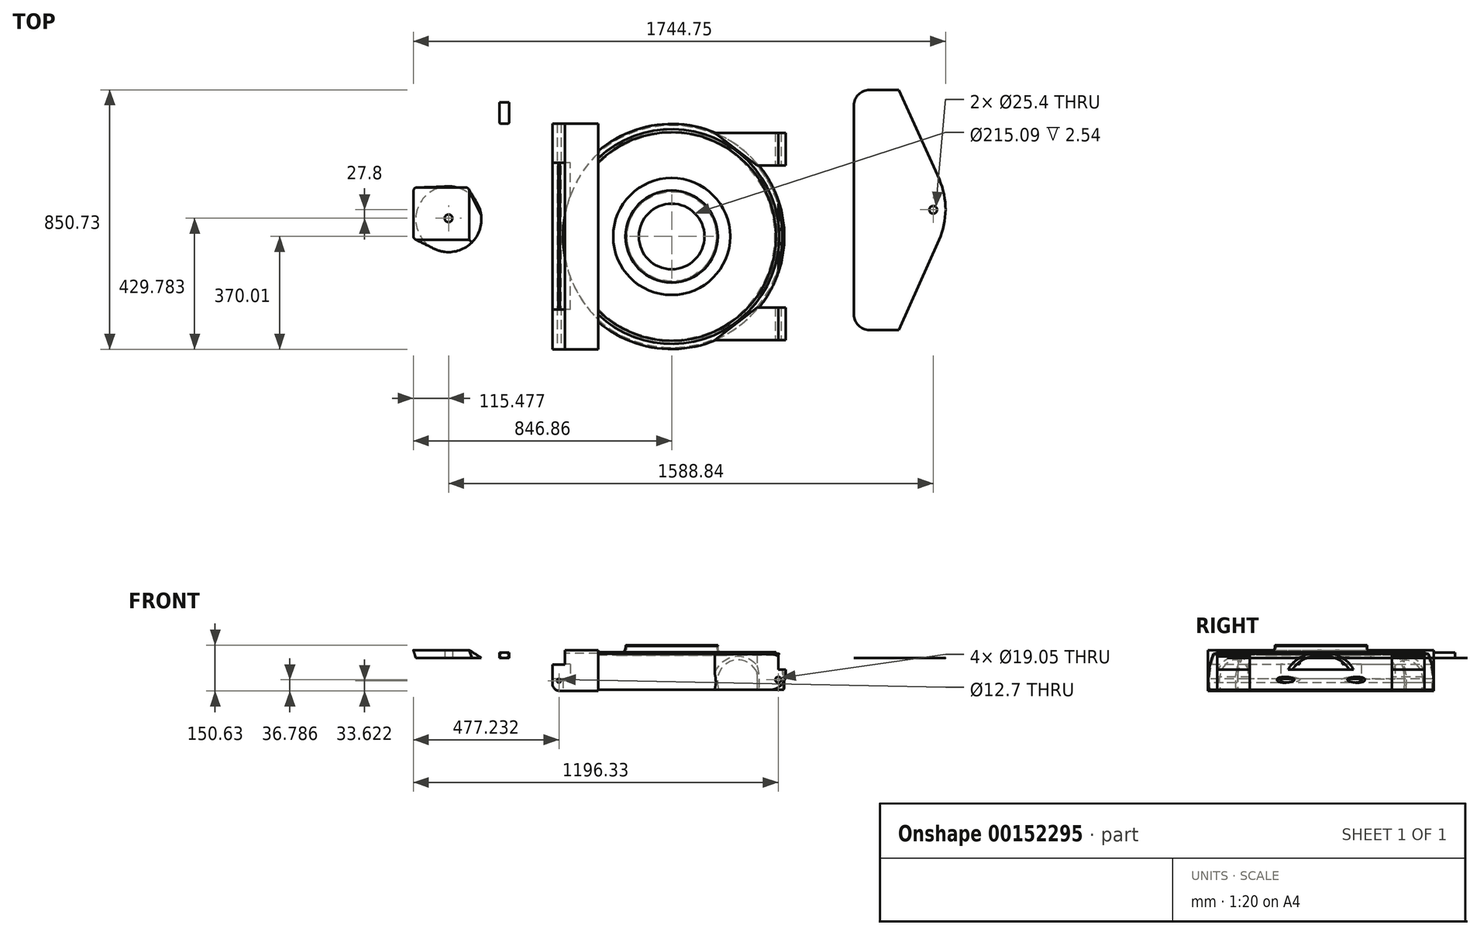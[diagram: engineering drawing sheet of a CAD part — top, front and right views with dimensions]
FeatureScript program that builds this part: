
annotation { "Feature Type Name" : "Feature", "Feature Type Description" : "" }
export const myFeature = defineFeature(function(context is Context, id is Id, definition is map)
    precondition{}
    {
        {
            var Q0;
            Q0=qCreatedBy(makeId("Front.planeOp"),FACE);
            var sketch = newSketch(context, id + "F0", { "sketchPlane" : qUnion([Q0])});
            skArc(sketch, "E0", {"start": v(88.44, -104.18) * mm, "mid": v(87.74, -44.08) * mm, "end": v(72.73, 14.12) * mm});
            skLineSegment(sketch, "E1", {"start": v(72.73, 14.12) * mm, "end": v(62.92, 14.12) * mm});
            skLineSegment(sketch, "E2", {"start": v(62.92, 14.12) * mm, "end": v(62.92, 19.16) * mm});
            skLineSegment(sketch, "E3", {"start": v(62.92, 19.16) * mm, "end": v(-87.54, 19.16) * mm});
            skArc(sketch, "E4", {"start": v(-127.97, 39.68) * mm, "mid": v(-115.17, 14.8) * mm, "end": v(-87.54, 19.16) * mm});
            skArc(sketch, "E5.0", {"start": v(84.66, -103.77) * mm, "mid": v(84.13, -45.87) * mm, "end": v(70.11, 10.3) * mm});
            skArc(sketch, "E5.1", {"start": v(-131.82, 39.68) * mm, "mid": v(-117.36, 11.64) * mm, "end": v(-86.03, 15.35) * mm});
            skLineSegment(sketch, "E5.2", {"start": v(59.1, 15.35) * mm, "end": v(-86.03, 15.35) * mm});
            skLineSegment(sketch, "E5.3", {"start": v(59.1, 10.3) * mm, "end": v(59.1, 15.35) * mm});
            skLineSegment(sketch, "E5.4", {"start": v(70.11, 10.3) * mm, "end": v(59.1, 10.3) * mm});
            skLineSegment(sketch, "E6", {"start": v(84.66, -103.77) * mm, "end": v(88.44, -104.18) * mm});
            skLineSegment(sketch, "E7", {"start": v(-127.97, 39.68) * mm, "end": v(-131.82, 39.68) * mm});
            skSolve(sketch);
        }
        {
            var Q0;
            Q0=qCreatedBy(makeId("Top.planeOp"),FACE);
            var sketch = newSketch(context, id + "F1", { "sketchPlane" : qUnion([Q0])});
            skCircle(sketch, "E8", {"center": v(-279.4, 0) * mm, "radius": 278.33 * mm});
            skSolve(sketch);
        }
        {
            var Q0;
            Q0 = qSketchRegion(id + "F0", true);
            var Q1;
            Q1=sQuery(id+"F1.wireOp",EDGE,"E8");
            sweep(context, id + "F2", {"profiles" : qUnion([Q0]), "path" : qUnion([Q1])});
        }
        {
            var Q0;
            Q0=makeQuery(id+"F2.opSweep","SWEPT_FACE",FACE,{"disambiguationData":[OSD([sQuery(id+"F0.wireOp",EDGE,"E7"),sQuery(id+"F1.wireOp",EDGE,"E8")])]});
            var sketch = newSketch(context, id + "F3", { "sketchPlane" : qUnion([Q0])});
            skCircle(sketch, "E9", {"center": v(-279.4, 0) * mm, "radius": 151.23 * mm});
            skCircle(sketch, "E10.0", {"center": v(-279.4, 0) * mm, "radius": 107.54 * mm});
            skSolve(sketch);
        }
        {
            var Q0;
            Q0 = qSketchRegion(id + "F3", true);
            extrude(context, id + "F4", {"entities" : qUnion([Q0]), "operationType" : NewBodyOperationType.ADD, "depth" : 2.54 * mm});
        }
        {
            var Q0;
            Q0=qCreatedBy(makeId("Right.planeOp"),FACE);
            cPlane(context, id + "F5", {"entities" : qUnion([Q0]), "cplaneType" : CPlaneType.OFFSET, "offset" : 520.7 * mm, "oppositeDirection" : true, "width" : 152.4 * mm, "height" : 152.4 * mm});
        }
        {
            var Q0;
            Q0=qCreatedBy(id+"F5.planeOp",FACE);
            var sketch = newSketch(context, id + "F6", { "sketchPlane" : qUnion([Q0])});
            skLineSegment(sketch, "E11.bottom", {"start": v(-370.01, 24.86) * mm, "end": v(370.01, 24.86) * mm});
            skLineSegment(sketch, "E11.top", {"start": v(-370.01, -108.4) * mm, "end": v(370.01, -108.4) * mm});
            skLineSegment(sketch, "E11.left", {"start": v(-370.01, 24.86) * mm, "end": v(-370.01, -108.4) * mm});
            skLineSegment(sketch, "E11.right", {"start": v(370.01, 24.86) * mm, "end": v(370.01, -108.4) * mm});
            skPoint(sketch, "E11.middle", {"position": v(0, -41.77) * mm});
            skSolve(sketch);
        }
        {
            var Q0;
            Q0 = qSketchRegion(id + "F6", true);
            extrude(context, id + "F7", {"entities" : qUnion([Q0]), "operationType" : NewBodyOperationType.ADD, "oppositeDirection" : true, "depth" : 149.86 * mm});
        }
        {
            var Q0;
            Q0=qCreatedBy(makeId("Top.planeOp"),FACE);
            var sketch = newSketch(context, id + "F8", { "sketchPlane" : qUnion([Q0])});
            skLineSegment(sketch, "E12", {"start": v(-137.9, 339.8) * mm, "end": v(94.35, 339.8) * mm});
            skLineSegment(sketch, "E13", {"start": v(94.35, 339.8) * mm, "end": v(94.35, 232.77) * mm});
            skLineSegment(sketch, "E14", {"start": v(94.35, 232.77) * mm, "end": v(0, 232.77) * mm});
            skLineSegment(sketch, "E15", {"start": v(0, 232.77) * mm, "end": v(-137.9, 339.8) * mm});
            skLineSegment(sketch, "E16", {"start": v(151.44, 0) * mm, "end": v(108.1, 0) * mm});
            skLineSegment(sketch, "E17.MirrorCS", {"start": v(0, -232.77) * mm, "end": v(-137.9, -339.8) * mm});
            skLineSegment(sketch, "E18.MirrorCS", {"start": v(94.35, -232.77) * mm, "end": v(0, -232.77) * mm});
            skLineSegment(sketch, "E19.MirrorCS", {"start": v(-137.9, -339.8) * mm, "end": v(94.35, -339.8) * mm});
            skLineSegment(sketch, "E20.MirrorCS", {"start": v(94.35, -339.8) * mm, "end": v(94.35, -232.77) * mm});
            skSolve(sketch);
        }
        {
            var Q0;
            Q0 = qSketchRegion(id + "F8", true);
            extrude(context, id + "F9", {"entities" : qUnion([Q0]), "operationType" : NewBodyOperationType.ADD, "depth" : 12.7 * mm, "hasSecondDirection" : true, "secondDirectionOppositeDirection" : true, "secondDirectionDepth" : 104.14 * mm});
        }
        {
            var Q0;
            Q0=makeQuery(id+"F7.opExtrude","SWEPT_FACE",FACE,{"disambiguationData":[OSD([sQuery(id+"F6.wireOp",EDGE,"E11.left")])]});
            var sketch = newSketch(context, id + "F10", { "sketchPlane" : qUnion([Q0])});
            skLineSegment(sketch, "E21.bottom", {"start": v(-672.04, 26) * mm, "end": v(-629.2, 26) * mm});
            skLineSegment(sketch, "E21.top", {"start": v(-672.04, -21.44) * mm, "end": v(-629.2, -21.44) * mm});
            skLineSegment(sketch, "E21.left", {"start": v(-672.04, 26) * mm, "end": v(-672.04, -21.44) * mm});
            skLineSegment(sketch, "E21.right", {"start": v(-629.2, 26) * mm, "end": v(-629.2, -21.44) * mm});
            skSolve(sketch);
        }
        {
            var Q0;
            Q0 = qSketchRegion(id + "F10", true);
            extrude(context, id + "F11", {"entities" : qUnion([Q0]), "operationType" : NewBodyOperationType.REMOVE, "endBound" : BoundingType.THROUGH_ALL, "oppositeDirection" : true, "depth" : 25.4 * mm});
        }
        {
            var Q0;
            Q0=makeQuery(id+"F7.opExtrude","SWEPT_FACE",FACE,{"disambiguationData":[OSD([sQuery(id+"F6.wireOp",EDGE,"E11.left")])]});
            var sketch = newSketch(context, id + "F12", { "sketchPlane" : qUnion([Q0])});
            skCircle(sketch, "E22", {"center": v(-649.03, -74.79) * mm, "radius": 6.35 * mm});
            skPoint(sketch, "E22.centerSnap0", {"position": v(-649.59, -74.79) * mm});
            skSolve(sketch);
        }
        {
            var Q0;
            Q0 = qSketchRegion(id + "F12", true);
            extrude(context, id + "F13", {"entities" : qUnion([Q0]), "operationType" : NewBodyOperationType.REMOVE, "endBound" : BoundingType.THROUGH_ALL, "oppositeDirection" : true, "depth" : 25.4 * mm});
        }
        {
            var Q0;
            {var subQ0=sQuery(id+"F8.wireOp",EDGE,"E20.MirrorCS");var subQ1=sQuery(id+"F8.wireOp",EDGE,"E19.MirrorCS");Q0=makeQuery(id+"F9.boolean.opBoolean","SPLIT",FACE,{"disambiguationData":[TD([makeQuery(id+"F9.opExtrude","SWEPT_FACE",FACE,{"disambiguationData":[OSD([subQ0])]})])],"derivedFrom":makeQuery(id+"F9.opExtrude","SWEPT_FACE",FACE,{"disambiguationData":[OSD([subQ1])]})});}
            var sketch = newSketch(context, id + "F14", { "sketchPlane" : qUnion([Q0])});
            skCircle(sketch, "E23", {"center": v(70.07, -71.62) * mm, "radius": 9.53 * mm});
            skSolve(sketch);
        }
        {
            var Q0;
            Q0 = qSketchRegion(id + "F14", true);
            extrude(context, id + "F15", {"entities" : qUnion([Q0]), "operationType" : NewBodyOperationType.REMOVE, "endBound" : BoundingType.THROUGH_ALL, "oppositeDirection" : true, "depth" : 25.4 * mm});
        }
        {
            var Q0;
            Q0=makeQuery(id+"F7.opExtrude","CAP_FACE",FACE,{"disambiguationData":[OSD([sQuery(id+"F6.wireOp",EDGE,"E11.bottom"),sQuery(id+"F6.wireOp",EDGE,"E11.top"),sQuery(id+"F6.wireOp",EDGE,"E11.left"),sQuery(id+"F6.wireOp",EDGE,"E11.right")])],"isStart":false});
            var sketch = newSketch(context, id + "F16", { "sketchPlane" : qUnion([Q0])});
            skLineSegment(sketch, "E24.bottom", {"start": v(239.3, -20.5) * mm, "end": v(-242.46, -20.5) * mm});
            skLineSegment(sketch, "E24.top", {"start": v(239.3, -68.97) * mm, "end": v(-242.46, -68.97) * mm});
            skLineSegment(sketch, "E24.left", {"start": v(239.3, -20.5) * mm, "end": v(239.3, -68.97) * mm});
            skLineSegment(sketch, "E24.right", {"start": v(-242.46, -20.5) * mm, "end": v(-242.46, -68.97) * mm});
            skPoint(sketch, "E24.middle", {"position": v(-1.58, -44.74) * mm});
            skPoint(sketch, "E24.middle.positionSnap0", {"position": v(256.96, -44.74) * mm});
            skPoint(sketch, "E24.middle.positionSnap1", {"position": v(-1.58, -21.44) * mm});
            skPoint(sketch, "E24.centerSnap0", {"position": v(273.05, -44.74) * mm});
            skPoint(sketch, "E24.centerSnap1", {"position": v(-1.58, -21.44) * mm});
            skSolve(sketch);
        }
        {
            var Q0;
            Q0 = qSketchRegion(id + "F16", true);
            extrude(context, id + "F17", {"entities" : qUnion([Q0]), "operationType" : NewBodyOperationType.REMOVE, "oppositeDirection" : true, "depth" : 58.42 * mm});
        }
        {
            var Q0;
            Q0=makeQuery(id+"F9.opExtrude","CAP_EDGE",EDGE,{"disambiguationData":[OSD([sQuery(id+"F8.wireOp",EDGE,"E13")])],"isStart":false});
            var Q1;
            Q1=makeQuery(id+"F9.opExtrude","CAP_EDGE",EDGE,{"disambiguationData":[OSD([sQuery(id+"F8.wireOp",EDGE,"E13")])],"isStart":true});
            var Q2;
            Q2=makeQuery(id+"F9.opExtrude","CAP_EDGE",EDGE,{"disambiguationData":[OSD([sQuery(id+"F8.wireOp",EDGE,"E20.MirrorCS")])],"isStart":false});
            var Q3;
            Q3=makeQuery(id+"F9.opExtrude","CAP_EDGE",EDGE,{"disambiguationData":[OSD([sQuery(id+"F8.wireOp",EDGE,"E20.MirrorCS")])],"isStart":true});
            fillet(context, id + "F18", {"entities" : qUnion([Q0, Q1, Q2, Q3]), "radius" : 50.8 * mm, "tangentPropagation" : true, "allowEdgeOverflow" : false});
        }
        {
            var Q0;
            {var subQ0=sQuery(id+"F8.wireOp",EDGE,"E20.MirrorCS");var subQ1=sQuery(id+"F8.wireOp",EDGE,"E19.MirrorCS");Q0=makeQuery(id+"F9.boolean.opBoolean","SPLIT",FACE,{"disambiguationData":[TD([makeQuery(id+"F9.opExtrude","SWEPT_FACE",FACE,{"disambiguationData":[OSD([subQ0])]})])],"derivedFrom":makeQuery(id+"F9.opExtrude","SWEPT_FACE",FACE,{"disambiguationData":[OSD([subQ1])]})});}
            var sketch = newSketch(context, id + "F19", { "sketchPlane" : qUnion([Q0])});
            skLineSegment(sketch, "E25.bottom", {"start": v(94.35, -38.1) * mm, "end": v(70.8, -38.1) * mm});
            skLineSegment(sketch, "E25.top", {"start": v(94.35, 12.7) * mm, "end": v(70.8, 12.7) * mm});
            skLineSegment(sketch, "E25.left", {"start": v(94.35, -38.1) * mm, "end": v(94.35, 12.7) * mm});
            skLineSegment(sketch, "E25.right", {"start": v(70.8, -38.1) * mm, "end": v(70.8, 12.7) * mm});
            skSolve(sketch);
        }
        {
            var Q0;
            {var subQ0=sQuery(id+"F10.wireOp",EDGE,"E21.top");Q0=makeQuery(id+"F17.boolean.opBoolean","SPLIT",EDGE,{"disambiguationData":[TD([makeQuery(id+"F17.opExtrude","SWEPT_FACE",FACE,{"disambiguationData":[OSD([sQuery(id+"F16.wireOp",EDGE,"E24.right")])]})])],"derivedFrom":makeQuery(id+"F11.boolean.opBoolean","COPY",EDGE,{"derivedFrom":makeQuery(id+"F11.opExtrude","SWEPT_EDGE",EDGE,{"disambiguationData":[OSD([sQuery(id+"Fj7kD9DFQNtqFVv_1.wireOp",EDGE,"BMaBq8M4-cvh5-u96s-fvNz-bmABEU0iJNI0.left"),subQ0,sQuery(id+"F10.wireOp",EDGE,"E21.left")])]})})});}
            var Q1;
            {var subQ0=sQuery(id+"F6.wireOp",EDGE,"E11.top");Q1=makeQuery(id+"F17.boolean.opBoolean","SPLIT",EDGE,{"disambiguationData":[TD([makeQuery(id+"F17.opExtrude","SWEPT_FACE",FACE,{"disambiguationData":[OSD([sQuery(id+"F16.wireOp",EDGE,"E24.right")])]})])],"derivedFrom":makeQuery(id+"F7.opExtrude","CAP_EDGE",EDGE,{"disambiguationData":[OSD([subQ0])],"isStart":false})});}
            var Q2;
            {var subQ0=sQuery(id+"Fj7kD9DFQNtqFVv_1.wireOp",EDGE,"BMaBq8M4-cvh5-u96s-fvNz-bmABEU0iJNI0.left");var subQ1=sQuery(id+"F10.wireOp",EDGE,"E21.top");Q2=makeQuery(id+"F17.boolean.opBoolean","SPLIT",EDGE,{"disambiguationData":[TD([makeQuery(id+"F17.opExtrude","SWEPT_FACE",FACE,{"disambiguationData":[OSD([sQuery(id+"F16.wireOp",EDGE,"E24.left")])]})])],"derivedFrom":makeQuery(id+"F11.boolean.opBoolean","COPY",EDGE,{"derivedFrom":makeQuery(id+"F11.opExtrude","SWEPT_EDGE",EDGE,{"disambiguationData":[OSD([subQ0,subQ1,sQuery(id+"F10.wireOp",EDGE,"E21.left")])]})})});}
            var Q3;
            {var subQ0=sQuery(id+"F6.wireOp",EDGE,"E11.top");Q3=makeQuery(id+"F17.boolean.opBoolean","SPLIT",EDGE,{"disambiguationData":[TD([makeQuery(id+"F17.opExtrude","SWEPT_FACE",FACE,{"disambiguationData":[OSD([sQuery(id+"F16.wireOp",EDGE,"E24.left")])]})])],"derivedFrom":makeQuery(id+"F7.opExtrude","CAP_EDGE",EDGE,{"disambiguationData":[OSD([subQ0])],"isStart":false})});}
            fillet(context, id + "F20", {"entities" : qUnion([Q0, Q1, Q2, Q3]), "radius" : 25.4 * mm, "tangentPropagation" : true, "allowEdgeOverflow" : false});
        }
        {
            var Q0;
            Q0 = qSketchRegion(id + "F19", true);
            extrude(context, id + "F21", {"entities" : qUnion([Q0]), "operationType" : NewBodyOperationType.REMOVE, "endBound" : BoundingType.THROUGH_ALL, "oppositeDirection" : true, "depth" : 25.4 * mm});
        }
        {
            var Q0;
            Q0=qCreatedBy(makeId("Top.planeOp"),FACE);
            var sketch = newSketch(context, id + "F22", { "sketchPlane" : qUnion([Q0])});
            skLineSegment(sketch, "E26.bottom", {"start": v(697.74, 480.72) * mm, "end": v(369, 480.72) * mm});
            skLineSegment(sketch, "E26.top", {"start": v(697.74, -306.68) * mm, "end": v(369, -306.68) * mm});
            skLineSegment(sketch, "E26.left", {"start": v(748.54, 429.92) * mm, "end": v(748.54, -255.88) * mm});
            skLineSegment(sketch, "E26.right", {"start": v(318.2, 429.92) * mm, "end": v(318.2, -255.88) * mm});
            skPoint(sketch, "E26.middle", {"position": v(533.37, 87.02) * mm});
            skPoint(sketch, "E27.visualSharp", {"position": v(318.2, 480.72) * mm});
            skArc(sketch, "E27.filletArc", {"start": v(369, 480.72) * mm, "mid": v(333.08, 465.85) * mm, "end": v(318.2, 429.92) * mm});
            skPoint(sketch, "E28.visualSharp", {"position": v(318.2, -306.68) * mm});
            skArc(sketch, "E28.filletArc", {"start": v(318.2, -255.88) * mm, "mid": v(333.08, -291.8) * mm, "end": v(369, -306.68) * mm});
            skPoint(sketch, "E29.visualSharp", {"position": v(748.54, -306.68) * mm});
            skArc(sketch, "E29.filletArc", {"start": v(697.74, -306.68) * mm, "mid": v(733.66, -291.8) * mm, "end": v(748.54, -255.88) * mm});
            skPoint(sketch, "E30.visualSharp", {"position": v(748.54, 480.72) * mm});
            skArc(sketch, "E30.filletArc", {"start": v(748.54, 429.92) * mm, "mid": v(733.66, 465.85) * mm, "end": v(697.74, 480.72) * mm});
            skPoint(sketch, "E31.centerSnap0", {"position": v(748.54, 87.02) * mm});
            skLineSegment(sketch, "E32", {"start": v(598.04, 186.6) * mm, "end": v(465.43, 480.72) * mm});
            skLineSegment(sketch, "E33", {"start": v(597.23, -11.28) * mm, "end": v(465.43, -306.68) * mm});
            skArc(sketch, "E34", {"start": v(597.23, -11.28) * mm, "mid": v(618.5, 87.57) * mm, "end": v(598.04, 186.6) * mm});
            skSolve(sketch);
        }
        {
            var Q0;
            Q0=makeQuery(id+"F22.imprint","IMPRINT",FACE,{"disambiguationData":[TD([[makeQuery(id+"F22.imprint","IMPRINT",EDGE,{"derivedFrom":sQuery(id+"F22.wireOp",EDGE,"E26.right")}),1.0]])]});
            extrude(context, id + "F23", {"entities" : qUnion([Q0]), "depth" : 15 / 812.8 * mm});
        }
        {
            var Q0;
            Q0=qCreatedBy(makeId("Top.planeOp"),FACE);
            var sketch = newSketch(context, id + "F24", { "sketchPlane" : qUnion([Q0])});
            skLineSegment(sketch, "E35.bottom", {"start": v(-812.23, 369.7) * mm, "end": v(-844.23, 369.7) * mm});
            skLineSegment(sketch, "E35.top", {"start": v(-812.23, 439.7) * mm, "end": v(-844.23, 439.7) * mm});
            skLineSegment(sketch, "E35.left", {"start": v(-812.23, 369.7) * mm, "end": v(-812.23, 439.7) * mm});
            skLineSegment(sketch, "E35.right", {"start": v(-844.23, 369.7) * mm, "end": v(-844.23, 439.7) * mm});
            skPoint(sketch, "E35.middle", {"position": v(-828.23, 404.7) * mm});
            skSolve(sketch);
        }
        {
            var Q0;
            Q0 = qSketchRegion(id + "F24", true);
            extrude(context, id + "F25", {"entities" : qUnion([Q0]), "depth" : 17 * mm});
        }
        {
            var Q0;
            Q0=makeQuery(id+"F25.opExtrude","CAP_EDGE",EDGE,{"disambiguationData":[OSD([sQuery(id+"F24.wireOp",EDGE,"E35.bottom")])],"isStart":false});
            var Q1;
            Q1=makeQuery(id+"F25.opExtrude","SWEPT_EDGE",EDGE,{"disambiguationData":[OSD([sQuery(id+"F24.wireOp",EDGE,"E35.bottom"),sQuery(id+"F24.wireOp",EDGE,"E35.left")])]});
            var Q2;
            Q2=makeQuery(id+"F25.opExtrude","SWEPT_EDGE",EDGE,{"disambiguationData":[OSD([sQuery(id+"F24.wireOp",EDGE,"E35.bottom"),sQuery(id+"F24.wireOp",EDGE,"E35.right")])]});
            var Q3;
            Q3=makeQuery(id+"F25.opExtrude","CAP_EDGE",EDGE,{"disambiguationData":[OSD([sQuery(id+"F24.wireOp",EDGE,"E35.bottom")])],"isStart":true});
            fillet(context, id + "F26", {"entities" : qUnion([Q0, Q1, Q2, Q3]), "radius" : 5.08 * mm, "tangentPropagation" : true, "allowEdgeOverflow" : false});
        }
        {
            var Q0;
            Q0=qCreatedBy(makeId("Top.planeOp"),FACE);
            var sketch = newSketch(context, id + "F27", { "sketchPlane" : qUnion([Q0])});
            skCircle(sketch, "E36", {"center": v(-1010.75, 56.6) * mm, "radius": 107.68 * mm});
            skSolve(sketch);
        }
        {
            var Q0;
            Q0=qCreatedBy(makeId("Top.planeOp"),FACE);
            cPlane(context, id + "F28", {"entities" : qUnion([Q0]), "cplaneType" : CPlaneType.OFFSET, "offset" : 25.4 * mm, "width" : 152.4 * mm, "height" : 152.4 * mm});
        }
        {
            var Q0;
            Q0=qCreatedBy(id+"F28.planeOp",FACE);
            var sketch = newSketch(context, id + "F29", { "sketchPlane" : qUnion([Q0])});
            skLineSegment(sketch, "E37.bottom", {"start": v(-942.74, -11.42) * mm, "end": v(-1113.56, -11.42) * mm});
            skLineSegment(sketch, "E37.top", {"start": v(-955.44, 161.03) * mm, "end": v(-1113.56, 161.03) * mm});
            skLineSegment(sketch, "E37.left", {"start": v(-942.74, -11.42) * mm, "end": v(-942.74, 148.33) * mm});
            skLineSegment(sketch, "E37.right", {"start": v(-1126.26, 1.28) * mm, "end": v(-1126.26, 148.33) * mm});
            skPoint(sketch, "E38.visualSharp", {"position": v(-1126.26, 161.03) * mm});
            skArc(sketch, "E38.filletArc", {"start": v(-1113.56, 161.03) * mm, "mid": v(-1122.54, 157.31) * mm, "end": v(-1126.26, 148.33) * mm});
            skPoint(sketch, "E39.visualSharp", {"position": v(-1126.26, -11.42) * mm});
            skArc(sketch, "E39.filletArc", {"start": v(-1126.26, 1.28) * mm, "mid": v(-1122.54, -7.7) * mm, "end": v(-1113.56, -11.42) * mm});
            skPoint(sketch, "E40.visualSharp", {"position": v(-942.74, 161.03) * mm});
            skArc(sketch, "E40.filletArc", {"start": v(-942.74, 148.33) * mm, "mid": v(-946.46, 157.31) * mm, "end": v(-955.44, 161.03) * mm});
            skSolve(sketch);
        }
        {
            var Q0;
            Q0=makeQuery(id+"F27.imprint","IMPRINT",FACE,{"disambiguationData":[TD([[makeQuery(id+"F27.imprint","IMPRINT",EDGE,{"derivedFrom":sQuery(id+"F27.wireOp",EDGE,"E36")}),1.0]])]});
            var Q1;
            Q1=makeQuery(id+"F29.imprint","IMPRINT",FACE,{"disambiguationData":[TD([[makeQuery(id+"F29.imprint","IMPRINT",EDGE,{"derivedFrom":sQuery(id+"F29.wireOp",EDGE,"E37.bottom")}),-1.0]])]});
            loft(context, id + "F30", {"sheetProfilesArray" : [{ "sheetProfileEntities" : qUnion([Q0]) }, { "sheetProfileEntities" : qUnion([Q1]) }]});
        }
        {
            var Q0;
            Q0=makeQuery(id+"F30.opLoft","CAP_FACE",FACE,{"disambiguationData":[OSD([makeQuery(id+"F27.imprint","IMPRINT",FACE,{"disambiguationData":[TD([[makeQuery(id+"F27.imprint","IMPRINT",EDGE,{"derivedFrom":sQuery(id+"F27.wireOp",EDGE,"E36")}),1.0]])]})])],"isStart":true});
            var sketch = newSketch(context, id + "F31", { "sketchPlane" : qUnion([Q0])});
            skCircle(sketch, "E41", {"center": v(-1010.78, -59.77) * mm, "radius": 12.7 * mm});
            skSolve(sketch);
        }
        {
            var Q0;
            Q0 = qSketchRegion(id + "F31", true);
            extrude(context, id + "F32", {"entities" : qUnion([Q0]), "operationType" : NewBodyOperationType.REMOVE, "endBound" : BoundingType.THROUGH_ALL, "oppositeDirection" : true, "depth" : 25.4 * mm});
        }
        {
            var Q0;
            Q0=makeQuery(id+"F23.opExtrude","CAP_FACE",FACE,{"disambiguationData":[OSD([sQuery(id+"F22.wireOp",EDGE,"E26.right"),sQuery(id+"F22.wireOp",EDGE,"E27.filletArc"),sQuery(id+"F22.wireOp",EDGE,"E28.filletArc"),sQuery(id+"F22.wireOp",EDGE,"eMgaidv2-KLgX-WZuE-Hx3V-rEoQZ6ZShemP"),sQuery(id+"F22.wireOp",EDGE,"epRaI4dx-vElg-Z5Uz-659u-VbMy61hDDhaH"),sQuery(id+"F22.wireOp",EDGE,"ywktJ0Lj-dN2S-td1x-PMCd-5CncVOiI2QwK")])],"isStart":false});
            var sketch = newSketch(context, id + "F33", { "sketchPlane" : qUnion([Q0])});
            skCircle(sketch, "E42", {"center": v(578.06, 87.57) * mm, "radius": 12.7 * mm});
            skPoint(sketch, "E43", {"position": v(618.5, 87.57) * mm});
            skSolve(sketch);
        }
        {
            var Q0;
            Q0 = qSketchRegion(id + "F33", true);
            extrude(context, id + "F34", {"entities" : qUnion([Q0]), "operationType" : NewBodyOperationType.REMOVE, "endBound" : BoundingType.THROUGH_ALL, "oppositeDirection" : true, "depth" : 25.4 * mm});
        }
        {
            var Q0;
            Q0=makeQuery(id+"F7.opExtrude","SWEPT_FACE",FACE,{"disambiguationData":[OSD([sQuery(id+"F6.wireOp",EDGE,"E11.top")])]});
            var sketch = newSketch(context, id + "F35", { "sketchPlane" : qUnion([Q0])});
            skArc(sketch, "E44", {"start": v(-520.7, 272.46) * mm, "mid": v(-635.72, -0.14) * mm, "end": v(-520.7, -272.74) * mm});
            skLineSegment(sketch, "E45", {"start": v(-520.7, 272.46) * mm, "end": v(-520.7, -272.74) * mm});
            skSolve(sketch);
        }
        {
            var Q0;
            Q0 = qSketchRegion(id + "F35", true);
            var Q1;
            Q1=makeQuery(id+"F2.opSweep","SWEPT_FACE",FACE,{"disambiguationData":[OSD([sQuery(id+"F0.wireOp",EDGE,"E5.2"),sQuery(id+"F1.wireOp",EDGE,"E8")])]});
            extrude(context, id + "F36", {"entities" : qUnion([Q0]), "operationType" : NewBodyOperationType.REMOVE, "endBound" : BoundingType.UP_TO_SURFACE, "oppositeDirection" : true, "endBoundEntityFace" : qUnion([Q1]), "depth" : 25.4 * mm});
        }
    });
